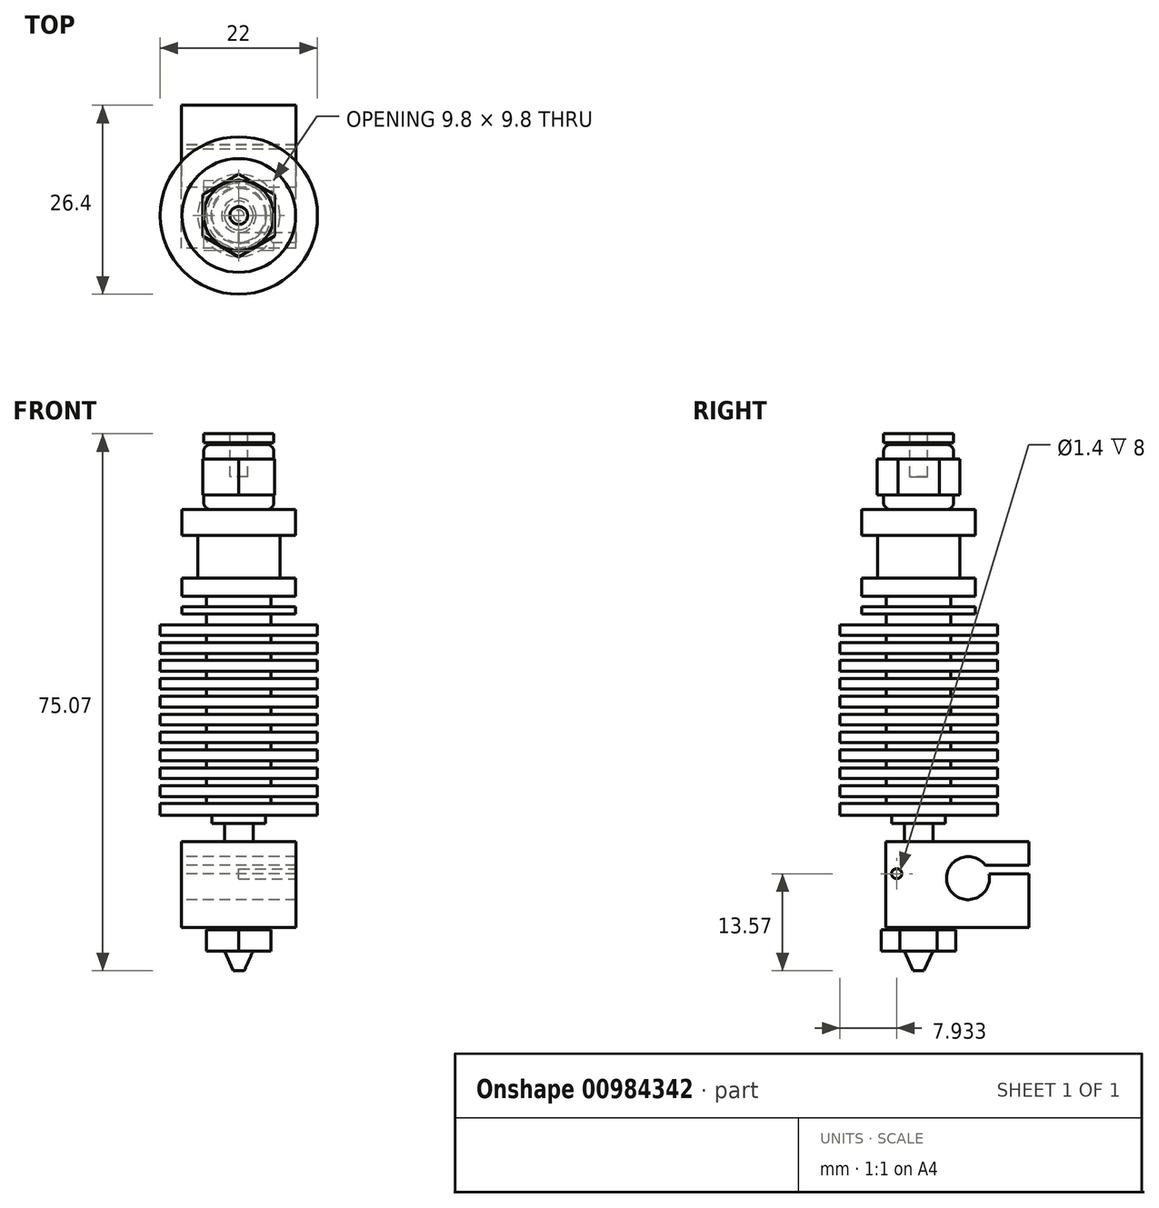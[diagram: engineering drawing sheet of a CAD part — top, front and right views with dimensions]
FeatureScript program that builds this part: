
annotation { "Feature Type Name" : "Feature", "Feature Type Description" : "" }
export const myFeature = defineFeature(function(context is Context, id is Id, definition is map)
    precondition{}
    {
        {
            var Q0;
            Q0=qCreatedBy(makeId("Top.planeOp"),FACE);
            cPlane(context, id + "F0", {"entities" : qUnion([Q0]), "cplaneType" : CPlaneType.OFFSET, "offset" : 3.7 * mm, "oppositeDirection" : true, "width" : 150 * mm, "height" : 150 * mm});
        }
        {
            var Q0;
            Q0=qCreatedBy(makeId("Top.planeOp"),FACE);
            cPlane(context, id + "F1", {"entities" : qUnion([Q0]), "cplaneType" : CPlaneType.OFFSET, "offset" : 19 * mm, "oppositeDirection" : true, "width" : 150 * mm, "height" : 150 * mm});
        }
        {
            var Q0;
            Q0=qCreatedBy(makeId("Top.planeOp"),FACE);
            cPlane(context, id + "F2", {"entities" : qUnion([Q0]), "cplaneType" : CPlaneType.OFFSET, "offset" : 47.25 * mm, "width" : 150 * mm, "height" : 150 * mm});
        }
        {
            var Q0;
            Q0=qCreatedBy(makeId("Front.planeOp"),FACE);
            var sketch = newSketch(context, id + "F3", { "sketchPlane" : qUnion([Q0])});
            skLineSegment(sketch, "E0", {"start": v(0, 0) * mm, "end": v(0, 42.7) * mm});
            skLineSegment(sketch, "E1", {"start": v(7.95, 42.7) * mm, "end": v(7.95, 39.1) * mm});
            skLineSegment(sketch, "E2", {"start": v(7.95, 39.1) * mm, "end": v(5.75, 39.1) * mm});
            skLineSegment(sketch, "E3", {"start": v(5.75, 39.1) * mm, "end": v(5.75, 33.1) * mm});
            skLineSegment(sketch, "E4", {"start": v(5.75, 33.1) * mm, "end": v(7.95, 33.1) * mm});
            skLineSegment(sketch, "E5", {"start": v(7.95, 33.1) * mm, "end": v(7.95, 30.6) * mm});
            skLineSegment(sketch, "E6", {"start": v(7.95, 30.6) * mm, "end": v(4.5, 30.6) * mm});
            skLineSegment(sketch, "E7", {"start": v(4.5, 30.6) * mm, "end": v(4.5, 29.1) * mm});
            skLineSegment(sketch, "E8", {"start": v(4.5, 29.1) * mm, "end": v(7.95, 29.1) * mm});
            skLineSegment(sketch, "E9", {"start": v(7.95, 29.1) * mm, "end": v(7.95, 28.1) * mm});
            skLineSegment(sketch, "E10", {"start": v(7.95, 28.1) * mm, "end": v(4.5, 28.1) * mm});
            skLineSegment(sketch, "E11", {"start": v(4.5, 28.1) * mm, "end": v(4.5, 26.6) * mm});
            skLineSegment(sketch, "E12", {"start": v(11, 26.6) * mm, "end": v(4.5, 26.6) * mm});
            skLineSegment(sketch, "E13.0", {"start": v(11, 25.1) * mm, "end": v(4.5, 25.1) * mm});
            skLineSegment(sketch, "E14.0", {"start": v(11, 24.1) * mm, "end": v(4.5, 24.1) * mm});
            skLineSegment(sketch, "E15.0", {"start": v(11, 22.6) * mm, "end": v(4.5, 22.6) * mm});
            skLineSegment(sketch, "E16.0", {"start": v(11, 21.6) * mm, "end": v(4.5, 21.6) * mm});
            skLineSegment(sketch, "E17.0", {"start": v(11, 20.1) * mm, "end": v(4.5, 20.1) * mm});
            skLineSegment(sketch, "E18.0", {"start": v(11, 19.1) * mm, "end": v(4.5, 19.1) * mm});
            skLineSegment(sketch, "E19.0", {"start": v(11, 17.6) * mm, "end": v(4.5, 17.6) * mm});
            skLineSegment(sketch, "E20", {"start": v(11, 16.6) * mm, "end": v(4.5, 16.6) * mm});
            skLineSegment(sketch, "E21.0", {"start": v(11, 15.1) * mm, "end": v(4.5, 15.1) * mm});
            skLineSegment(sketch, "E22.0", {"start": v(11, 14.1) * mm, "end": v(4.5, 14.1) * mm});
            skLineSegment(sketch, "E23.0", {"start": v(11, 12.6) * mm, "end": v(4.5, 12.6) * mm});
            skLineSegment(sketch, "E24", {"start": v(11, 11.6) * mm, "end": v(4.5, 11.6) * mm});
            skLineSegment(sketch, "E25.0", {"start": v(11, 10.1) * mm, "end": v(4.5, 10.1) * mm});
            skLineSegment(sketch, "E26.0", {"start": v(11, 9.1) * mm, "end": v(4.5, 9.1) * mm});
            skLineSegment(sketch, "E27.0", {"start": v(11, 7.6) * mm, "end": v(4.5, 7.6) * mm});
            skLineSegment(sketch, "E28", {"start": v(11, 6.6) * mm, "end": v(4.5, 6.6) * mm});
            skLineSegment(sketch, "E29.0", {"start": v(11, 5.1) * mm, "end": v(4.5, 5.1) * mm});
            skLineSegment(sketch, "E30.0", {"start": v(11, 4.1) * mm, "end": v(4.5, 4.1) * mm});
            skLineSegment(sketch, "E31.0", {"start": v(11, 2.6) * mm, "end": v(4.5, 2.6) * mm});
            skLineSegment(sketch, "E32.0", {"start": v(11, 1.6) * mm, "end": v(4.5, 1.6) * mm});
            skLineSegment(sketch, "E33", {"start": v(11, 26.6) * mm, "end": v(11, 25.1) * mm});
            skLineSegment(sketch, "E34", {"start": v(4.5, 25.1) * mm, "end": v(4.5, 24.1) * mm});
            skLineSegment(sketch, "E35", {"start": v(11, 24.1) * mm, "end": v(11, 22.6) * mm});
            skLineSegment(sketch, "E36", {"start": v(4.5, 22.6) * mm, "end": v(4.5, 21.6) * mm});
            skLineSegment(sketch, "E37", {"start": v(11, 21.6) * mm, "end": v(11, 20.1) * mm});
            skLineSegment(sketch, "E38", {"start": v(11, 19.1) * mm, "end": v(11, 17.6) * mm});
            skLineSegment(sketch, "E39", {"start": v(11, 16.6) * mm, "end": v(11, 15.1) * mm});
            skLineSegment(sketch, "E40", {"start": v(11, 14.1) * mm, "end": v(11, 12.6) * mm});
            skLineSegment(sketch, "E41", {"start": v(11, 11.6) * mm, "end": v(11, 10.1) * mm});
            skLineSegment(sketch, "E42", {"start": v(11, 9.1) * mm, "end": v(11, 7.6) * mm});
            skLineSegment(sketch, "E43", {"start": v(11, 6.6) * mm, "end": v(11, 5.1) * mm});
            skLineSegment(sketch, "E44", {"start": v(4.5, 20.1) * mm, "end": v(4.5, 19.1) * mm});
            skLineSegment(sketch, "E45", {"start": v(4.5, 17.6) * mm, "end": v(4.5, 16.6) * mm});
            skLineSegment(sketch, "E46", {"start": v(4.5, 15.1) * mm, "end": v(4.5, 14.1) * mm});
            skLineSegment(sketch, "E47", {"start": v(4.5, 12.6) * mm, "end": v(4.5, 11.6) * mm});
            skLineSegment(sketch, "E48", {"start": v(4.5, 10.1) * mm, "end": v(4.5, 9.1) * mm});
            skLineSegment(sketch, "E49", {"start": v(4.5, 7.6) * mm, "end": v(4.5, 6.6) * mm});
            skLineSegment(sketch, "E50", {"start": v(4.5, 5.1) * mm, "end": v(4.5, 4.1) * mm});
            skLineSegment(sketch, "E51", {"start": v(4.5, 2.6) * mm, "end": v(4.5, 1.6) * mm});
            skLineSegment(sketch, "E52", {"start": v(11, 4.1) * mm, "end": v(11, 2.6) * mm});
            skLineSegment(sketch, "E53", {"start": v(11, 1.6) * mm, "end": v(11, 0) * mm});
            skLineSegment(sketch, "E54", {"start": v(3.75, 0) * mm, "end": v(3.75, -1.2) * mm});
            skLineSegment(sketch, "E55", {"start": v(3.75, -1.2) * mm, "end": v(2, -1.2) * mm});
            skLineSegment(sketch, "E56", {"start": v(2, -1.2) * mm, "end": v(2, -19) * mm});
            skLineSegment(sketch, "E57", {"start": v(0, -21.77) * mm, "end": v(0.75, -21.77) * mm});
            skLineSegment(sketch, "E58", {"start": v(0.75, -21.77) * mm, "end": v(2, -19) * mm});
            skLineSegment(sketch, "E59", {"start": v(0, 0) * mm, "end": v(0, -21.77) * mm});
            skLineSegment(sketch, "E60", {"start": v(3.75, 0) * mm, "end": v(11, 0) * mm});
            skLineSegment(sketch, "E61", {"start": v(0, 42.7) * mm, "end": v(0, 51.8) * mm});
            skArc(sketch, "E62", {"start": v(4.9, 43.7) * mm, "mid": v(4.6, 43) * mm, "end": v(3.9, 42.7) * mm});
            skArc(sketch, "E63.MirrorCS", {"start": v(4.9, 50.8) * mm, "mid": v(4.6, 51.5) * mm, "end": v(3.9, 51.8) * mm});
            skLineSegment(sketch, "E64", {"start": v(4.9, 50.8) * mm, "end": v(4.9, 43.7) * mm});
            skLineSegment(sketch, "E65", {"start": v(3.9, 42.7) * mm, "end": v(7.95, 42.7) * mm});
            skLineSegment(sketch, "E66", {"start": v(4.9, 52.05) * mm, "end": v(4.9, 53.3) * mm});
            skLineSegment(sketch, "E67", {"start": v(4.9, 53.3) * mm, "end": v(0, 53.3) * mm});
            skLineSegment(sketch, "E68", {"start": v(0, 53.3) * mm, "end": v(0, 51.8) * mm});
            skLineSegment(sketch, "E69.0", {"start": v(2.4, 51.8) * mm, "end": v(2.4, 52.05) * mm});
            skLineSegment(sketch, "E70", {"start": v(3.9, 51.8) * mm, "end": v(2.4, 51.8) * mm});
            skLineSegment(sketch, "E71", {"start": v(2.4, 52.05) * mm, "end": v(4.9, 52.05) * mm});
            skSolve(sketch);
        }
        {
            var Q0;
            Q0=qCreatedBy(makeId("Top.planeOp"),FACE);
            var sketch = newSketch(context, id + "F4", { "sketchPlane" : qUnion([Q0])});
            skCircle(sketch, "E72", {"center": v(0, 0) * mm, "radius": 3.75 * mm});
            skCircle(sketch, "E73", {"center": v(0, 0) * mm, "radius": 2 * mm});
            skSolve(sketch);
        }
        {
            var Q0;
            Q0=qCreatedBy(id+"F1.planeOp",FACE);
            var sketch = newSketch(context, id + "F5", { "sketchPlane" : qUnion([Q0])});
            skLineSegment(sketch, "E74.0", {"start": v(4.5, 2.6) * mm, "end": v(4.5, -2.6) * mm});
            skLineSegment(sketch, "E74.1", {"start": v(4.5, -2.6) * mm, "end": v(0, -5.2) * mm});
            skLineSegment(sketch, "E74.2", {"start": v(0, -5.2) * mm, "end": v(-4.5, -2.6) * mm});
            skLineSegment(sketch, "E74.3", {"start": v(-4.5, -2.6) * mm, "end": v(-4.5, 2.6) * mm});
            skLineSegment(sketch, "E74.4", {"start": v(-4.5, 2.6) * mm, "end": v(0, 5.2) * mm});
            skLineSegment(sketch, "E74.5", {"start": v(0, 5.2) * mm, "end": v(4.5, 2.6) * mm});
            skPoint(sketch, "E74.0.midPoint", {"position": v(4.5, 0) * mm});
            skSolve(sketch);
        }
        {
            var Q0;
            Q0=qCreatedBy(id+"F2.planeOp",FACE);
            var sketch = newSketch(context, id + "F6", { "sketchPlane" : qUnion([Q0])});
            skLineSegment(sketch, "E75.0", {"start": v(5, 2.89) * mm, "end": v(5, -2.89) * mm});
            skLineSegment(sketch, "E75.1", {"start": v(5, -2.89) * mm, "end": v(0, -5.77) * mm});
            skLineSegment(sketch, "E75.2", {"start": v(0, -5.77) * mm, "end": v(-5, -2.89) * mm});
            skLineSegment(sketch, "E75.3", {"start": v(-5, -2.89) * mm, "end": v(-5, 2.89) * mm});
            skLineSegment(sketch, "E75.4", {"start": v(-5, 2.89) * mm, "end": v(0, 5.77) * mm});
            skLineSegment(sketch, "E75.5", {"start": v(0, 5.77) * mm, "end": v(5, 2.89) * mm});
            skPoint(sketch, "E75.0.midPoint", {"position": v(5, 0) * mm});
            skCircle(sketch, "E76", {"center": v(0, 0) * mm, "radius": 1.25 * mm, "construction": true});
            skSolve(sketch);
        }
        {
            var Q0;
            Q0=qCreatedBy(makeId("Right.planeOp"),FACE);
            var sketch = newSketch(context, id + "F7", { "sketchPlane" : qUnion([Q0])});
            skLineSegment(sketch, "E77.bottom", {"start": v(-4.6, -3.7) * mm, "end": v(15.4, -3.7) * mm});
            skLineSegment(sketch, "E77.top", {"start": v(-4.6, -15.7) * mm, "end": v(15.4, -15.7) * mm});
            skLineSegment(sketch, "E77.left", {"start": v(-4.6, -3.7) * mm, "end": v(-4.6, -15.7) * mm});
            skLineSegment(sketch, "E77.right", {"start": v(15.4, -3.7) * mm, "end": v(15.4, -15.7) * mm});
            skLineSegment(sketch, "E78", {"start": v(15.4, -7) * mm, "end": v(9.29, -7) * mm});
            skLineSegment(sketch, "E79", {"start": v(15.4, -8.2) * mm, "end": v(9.84, -8.2) * mm});
            skCircle(sketch, "E80", {"center": v(-3.07, -8.2) * mm, "radius": 0.6 * mm, "construction": true});
            skArc(sketch, "E81", {"start": v(9.29, -7) * mm, "mid": v(4.17, -10.06) * mm, "end": v(9.84, -8.2) * mm});
            skSolve(sketch);
        }
        {
            var Q0;
            Q0=makeQuery(id+"F3.imprint","IMPRINT",FACE,{"disambiguationData":[TD([[makeQuery(id+"F3.imprint","IMPRINT",EDGE,{"derivedFrom":sQuery(id+"F3.wireOp",EDGE,"E0")}),-1.0]])]});
            var Q1;
            Q1=sQuery(id+"F3.wireOp",EDGE,"E0");
            revolve(context, id + "F8", {"entities" : qUnion([Q0]), "axis" : qUnion([Q1]), "revolveType" : RevolveType.FULL});
        }
        {
            var Q0;
            Q0=makeQuery(id+"F4.imprint","IMPRINT",FACE,{"disambiguationData":[TD([[makeQuery(id+"F4.imprint","IMPRINT",EDGE,{"derivedFrom":sQuery(id+"F4.wireOp",EDGE,"E72")}),1.0]])]});
            extrude(context, id + "F9", {"entities" : qUnion([Q0]), "operationType" : NewBodyOperationType.ADD, "oppositeDirection" : true, "depth" : 1.2 * mm});
        }
        {
            var Q0;
            Q0=makeQuery(id+"F4.imprint","IMPRINT",FACE,{"disambiguationData":[TD([[makeQuery(id+"F4.imprint","IMPRINT",EDGE,{"derivedFrom":sQuery(id+"F4.wireOp",EDGE,"E73")}),1.0]])]});
            extrude(context, id + "F10", {"entities" : qUnion([Q0]), "operationType" : NewBodyOperationType.ADD, "oppositeDirection" : true, "depth" : 3.7 * mm});
        }
        {
            var Q0;
            Q0=makeQuery(id+"F5.imprint","IMPRINT",FACE,{"disambiguationData":[TD([[makeQuery(id+"F5.imprint","IMPRINT",EDGE,{"derivedFrom":sQuery(id+"F5.wireOp",EDGE,"E74.0")}),-1.0]])]});
            extrude(context, id + "F11", {"entities" : qUnion([Q0]), "operationType" : NewBodyOperationType.ADD, "depth" : 3 * mm});
        }
        {
            var Q0;
            Q0=makeQuery(id+"F6.imprint","IMPRINT",FACE,{"disambiguationData":[TD([[makeQuery(id+"F6.imprint","IMPRINT",EDGE,{"derivedFrom":sQuery(id+"F6.wireOp",EDGE,"E75.0")}),-1.0]])]});
            extrude(context, id + "F12", {"entities" : qUnion([Q0]), "operationType" : NewBodyOperationType.ADD, "depth" : 5 * mm, "symmetric" : true});
        }
        {
            var Q0;
            {var subQ1=sQuery(id+"F7.wireOp",EDGE,"E77.bottom");Q0=makeQuery(id+"F7.imprint","IMPRINT",FACE,{"disambiguationData":[TD([[makeQuery(id+"F7.imprint","IMPRINT",EDGE,{"derivedFrom":subQ1}),-1.0]])]});}
            extrude(context, id + "F13", {"entities" : qUnion([Q0]), "operationType" : NewBodyOperationType.ADD, "depth" : 16 * mm, "symmetric" : true});
        }
        {
            var Q0;
            Q0=sQuery(id+"F6.wireOp",VERTEX,"E76.center");
            var Q1;
            Q1=makeQuery(id+"F8.opRevolve","SWEPT_BODY",BODY,{"disambiguationData":[OSD([sQuery(id+"F3.wireOp",EDGE,"E0"),sQuery(id+"F3.wireOp",EDGE,"E1"),sQuery(id+"F3.wireOp",EDGE,"E2"),sQuery(id+"F3.wireOp",EDGE,"E3"),sQuery(id+"F3.wireOp",EDGE,"E4"),sQuery(id+"F3.wireOp",EDGE,"E5"),sQuery(id+"F3.wireOp",EDGE,"E6"),sQuery(id+"F3.wireOp",EDGE,"E7"),sQuery(id+"F3.wireOp",EDGE,"E8"),sQuery(id+"F3.wireOp",EDGE,"E9"),sQuery(id+"F3.wireOp",EDGE,"E10"),sQuery(id+"F3.wireOp",EDGE,"E11"),sQuery(id+"F3.wireOp",EDGE,"E12"),sQuery(id+"F3.wireOp",EDGE,"E13.0"),sQuery(id+"F3.wireOp",EDGE,"E14.0"),sQuery(id+"F3.wireOp",EDGE,"E15.0"),sQuery(id+"F3.wireOp",EDGE,"E16.0"),sQuery(id+"F3.wireOp",EDGE,"E17.0"),sQuery(id+"F3.wireOp",EDGE,"E18.0"),sQuery(id+"F3.wireOp",EDGE,"E19.0"),sQuery(id+"F3.wireOp",EDGE,"E20"),sQuery(id+"F3.wireOp",EDGE,"E21.0"),sQuery(id+"F3.wireOp",EDGE,"E22.0"),sQuery(id+"F3.wireOp",EDGE,"E23.0"),sQuery(id+"F3.wireOp",EDGE,"E24"),sQuery(id+"F3.wireOp",EDGE,"E25.0"),sQuery(id+"F3.wireOp",EDGE,"E26.0"),sQuery(id+"F3.wireOp",EDGE,"E27.0"),sQuery(id+"F3.wireOp",EDGE,"E28"),sQuery(id+"F3.wireOp",EDGE,"E29.0"),sQuery(id+"F3.wireOp",EDGE,"E30.0"),sQuery(id+"F3.wireOp",EDGE,"E31.0"),sQuery(id+"F3.wireOp",EDGE,"E32.0"),sQuery(id+"F3.wireOp",EDGE,"E33"),sQuery(id+"F3.wireOp",EDGE,"E34"),sQuery(id+"F3.wireOp",EDGE,"E35"),sQuery(id+"F3.wireOp",EDGE,"E36"),sQuery(id+"F3.wireOp",EDGE,"E37"),sQuery(id+"F3.wireOp",EDGE,"E38"),sQuery(id+"F3.wireOp",EDGE,"E39"),sQuery(id+"F3.wireOp",EDGE,"E40"),sQuery(id+"F3.wireOp",EDGE,"E41"),sQuery(id+"F3.wireOp",EDGE,"E42"),sQuery(id+"F3.wireOp",EDGE,"E43"),sQuery(id+"F3.wireOp",EDGE,"E44"),sQuery(id+"F3.wireOp",EDGE,"E45"),sQuery(id+"F3.wireOp",EDGE,"E46"),sQuery(id+"F3.wireOp",EDGE,"E47"),sQuery(id+"F3.wireOp",EDGE,"E48"),sQuery(id+"F3.wireOp",EDGE,"E49"),sQuery(id+"F3.wireOp",EDGE,"E50"),sQuery(id+"F3.wireOp",EDGE,"E51"),sQuery(id+"F3.wireOp",EDGE,"E52"),sQuery(id+"F3.wireOp",EDGE,"E53"),sQuery(id+"F3.wireOp",EDGE,"E54"),sQuery(id+"F3.wireOp",EDGE,"E55"),sQuery(id+"F3.wireOp",EDGE,"E56"),sQuery(id+"F3.wireOp",EDGE,"E57"),sQuery(id+"F3.wireOp",EDGE,"E58"),sQuery(id+"F3.wireOp",EDGE,"E59"),sQuery(id+"F3.wireOp",EDGE,"E60"),sQuery(id+"F3.wireOp",EDGE,"E61"),sQuery(id+"F3.wireOp",EDGE,"E62"),sQuery(id+"F3.wireOp",EDGE,"E63.MirrorCS"),sQuery(id+"F3.wireOp",EDGE,"E64"),sQuery(id+"F3.wireOp",EDGE,"E65"),sQuery(id+"F3.wireOp",EDGE,"E66"),sQuery(id+"F3.wireOp",EDGE,"E67"),sQuery(id+"F3.wireOp",EDGE,"E68"),sQuery(id+"F3.wireOp",EDGE,"E69.0"),sQuery(id+"F3.wireOp",EDGE,"E70"),sQuery(id+"F3.wireOp",EDGE,"E71")])]});
            hole(context, id + "F14", {"style" : HoleStyle.SIMPLE, "endStyle" : HoleEndStyle.THROUGH, "oppositeDirection" : true, "holeDiameter" : 2.5 * mm, "isTappedThrough" : true, "tappedDepth" : 12 * mm, "tapClearance" : 3, "locations" : qUnion([Q0]), "scope" : qUnion([Q1])});
        }
        {
            var Q0;
            Q0=sQuery(id+"F7.wireOp",VERTEX,"E80.center");
            var Q1;
            Q1=makeQuery(id+"F8.opRevolve","SWEPT_BODY",BODY,{"disambiguationData":[OSD([sQuery(id+"F3.wireOp",EDGE,"E0"),sQuery(id+"F3.wireOp",EDGE,"E1"),sQuery(id+"F3.wireOp",EDGE,"E2"),sQuery(id+"F3.wireOp",EDGE,"E3"),sQuery(id+"F3.wireOp",EDGE,"E4"),sQuery(id+"F3.wireOp",EDGE,"E5"),sQuery(id+"F3.wireOp",EDGE,"E6"),sQuery(id+"F3.wireOp",EDGE,"E7"),sQuery(id+"F3.wireOp",EDGE,"E8"),sQuery(id+"F3.wireOp",EDGE,"E9"),sQuery(id+"F3.wireOp",EDGE,"E10"),sQuery(id+"F3.wireOp",EDGE,"E11"),sQuery(id+"F3.wireOp",EDGE,"E12"),sQuery(id+"F3.wireOp",EDGE,"E13.0"),sQuery(id+"F3.wireOp",EDGE,"E14.0"),sQuery(id+"F3.wireOp",EDGE,"E15.0"),sQuery(id+"F3.wireOp",EDGE,"E16.0"),sQuery(id+"F3.wireOp",EDGE,"E17.0"),sQuery(id+"F3.wireOp",EDGE,"E18.0"),sQuery(id+"F3.wireOp",EDGE,"E19.0"),sQuery(id+"F3.wireOp",EDGE,"E20"),sQuery(id+"F3.wireOp",EDGE,"E21.0"),sQuery(id+"F3.wireOp",EDGE,"E22.0"),sQuery(id+"F3.wireOp",EDGE,"E23.0"),sQuery(id+"F3.wireOp",EDGE,"E24"),sQuery(id+"F3.wireOp",EDGE,"E25.0"),sQuery(id+"F3.wireOp",EDGE,"E26.0"),sQuery(id+"F3.wireOp",EDGE,"E27.0"),sQuery(id+"F3.wireOp",EDGE,"E28"),sQuery(id+"F3.wireOp",EDGE,"E29.0"),sQuery(id+"F3.wireOp",EDGE,"E30.0"),sQuery(id+"F3.wireOp",EDGE,"E31.0"),sQuery(id+"F3.wireOp",EDGE,"E32.0"),sQuery(id+"F3.wireOp",EDGE,"E33"),sQuery(id+"F3.wireOp",EDGE,"E34"),sQuery(id+"F3.wireOp",EDGE,"E35"),sQuery(id+"F3.wireOp",EDGE,"E36"),sQuery(id+"F3.wireOp",EDGE,"E37"),sQuery(id+"F3.wireOp",EDGE,"E38"),sQuery(id+"F3.wireOp",EDGE,"E39"),sQuery(id+"F3.wireOp",EDGE,"E40"),sQuery(id+"F3.wireOp",EDGE,"E41"),sQuery(id+"F3.wireOp",EDGE,"E42"),sQuery(id+"F3.wireOp",EDGE,"E43"),sQuery(id+"F3.wireOp",EDGE,"E44"),sQuery(id+"F3.wireOp",EDGE,"E45"),sQuery(id+"F3.wireOp",EDGE,"E46"),sQuery(id+"F3.wireOp",EDGE,"E47"),sQuery(id+"F3.wireOp",EDGE,"E48"),sQuery(id+"F3.wireOp",EDGE,"E49"),sQuery(id+"F3.wireOp",EDGE,"E50"),sQuery(id+"F3.wireOp",EDGE,"E51"),sQuery(id+"F3.wireOp",EDGE,"E52"),sQuery(id+"F3.wireOp",EDGE,"E53"),sQuery(id+"F3.wireOp",EDGE,"E54"),sQuery(id+"F3.wireOp",EDGE,"E55"),sQuery(id+"F3.wireOp",EDGE,"E56"),sQuery(id+"F3.wireOp",EDGE,"E57"),sQuery(id+"F3.wireOp",EDGE,"E58"),sQuery(id+"F3.wireOp",EDGE,"E59"),sQuery(id+"F3.wireOp",EDGE,"E60"),sQuery(id+"F3.wireOp",EDGE,"E61"),sQuery(id+"F3.wireOp",EDGE,"E62"),sQuery(id+"F3.wireOp",EDGE,"E63.MirrorCS"),sQuery(id+"F3.wireOp",EDGE,"E64"),sQuery(id+"F3.wireOp",EDGE,"E65"),sQuery(id+"F3.wireOp",EDGE,"E66"),sQuery(id+"F3.wireOp",EDGE,"E67"),sQuery(id+"F3.wireOp",EDGE,"E68"),sQuery(id+"F3.wireOp",EDGE,"E69.0"),sQuery(id+"F3.wireOp",EDGE,"E70"),sQuery(id+"F3.wireOp",EDGE,"E71")])]});
            hole(context, id + "F15", {"style" : HoleStyle.SIMPLE, "endStyle" : HoleEndStyle.THROUGH, "oppositeDirection" : true, "holeDiameter" : 1.4 * mm, "isTappedThrough" : true, "tappedDepth" : 12 * mm, "tapClearance" : 3, "locations" : qUnion([Q0]), "scope" : qUnion([Q1])});
        }
    });
